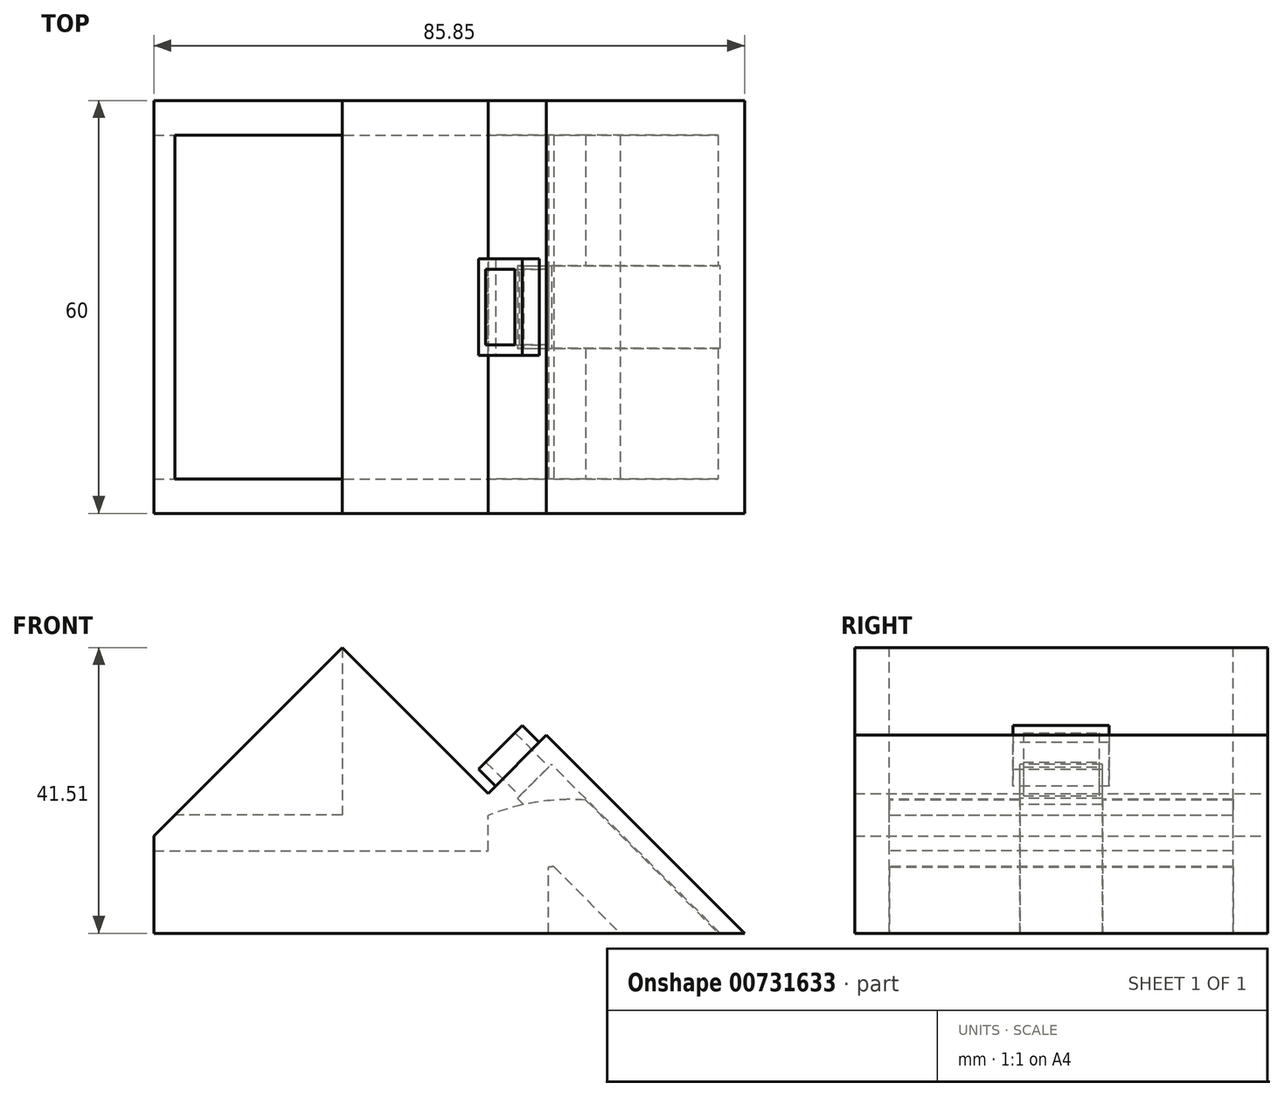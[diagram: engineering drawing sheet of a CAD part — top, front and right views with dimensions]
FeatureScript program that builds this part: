
annotation { "Feature Type Name" : "Feature", "Feature Type Description" : "" }
export const myFeature = defineFeature(function(context is Context, id is Id, definition is map)
    precondition{}
    {
        {
            var Q0;
            Q0=qCreatedBy(makeId("Front.planeOp"),FACE);
            var sketch = newSketch(context, id + "F0", { "sketchPlane" : qUnion([Q0])});
            skLineSegment(sketch, "E0", {"start": v(-35.85, 14.15) * mm, "end": v(-8.49, 41.51) * mm});
            skLineSegment(sketch, "E1", {"start": v(21.21, 28.79) * mm, "end": v(50, 0) * mm});
            skLineSegment(sketch, "E2", {"start": v(50, 0) * mm, "end": v(-35.85, 0) * mm});
            skLineSegment(sketch, "E3", {"start": v(-8.49, 41.51) * mm, "end": v(12.73, 20.3) * mm});
            skLineSegment(sketch, "E4", {"start": v(12.73, 20.3) * mm, "end": v(21.21, 28.79) * mm});
            skLineSegment(sketch, "E5", {"start": v(-35.85, 0) * mm, "end": v(-35.85, 14.15) * mm});
            skSolve(sketch);
        }
        {
            var Q0;
            Q0 = qSketchRegion(id + "F0", true);
            extrude(context, id + "F1", {"entities" : qUnion([Q0]), "endBound" : BoundingType.SYMMETRIC, "depth" : 60 * mm, "offsetDistance" : 25 * mm});
        }
        {
            var Q0;
            Q0=makeQuery(id+"F1.opExtrude","SWEPT_FACE",FACE,{"disambiguationData":[OSD([sQuery(id+"F0.wireOp",EDGE,"E4")])]});
            var sketch = newSketch(context, id + "F2", { "sketchPlane" : qUnion([Q0])});
            skPoint(sketch, "E6.middle.positionSnap0", {"position": v(0, 23.36) * mm});
            skPoint(sketch, "E6.centerSnap0", {"position": v(0, 23.36) * mm});
            skLineSegment(sketch, "E7.bottom", {"start": v(6, 32.86) * mm, "end": v(-6, 32.86) * mm});
            skLineSegment(sketch, "E7.top", {"start": v(6, 25.86) * mm, "end": v(-6, 25.86) * mm});
            skLineSegment(sketch, "E7.left", {"start": v(6, 32.86) * mm, "end": v(6, 25.86) * mm});
            skLineSegment(sketch, "E7.right", {"start": v(-6, 32.86) * mm, "end": v(-6, 25.86) * mm});
            skPoint(sketch, "E7.middle", {"position": v(0, 29.36) * mm});
            skPoint(sketch, "E7.middle.positionSnap0", {"position": v(-30, 29.36) * mm});
            skPoint(sketch, "E7.centerSnap0", {"position": v(-30, 29.36) * mm});
            skSolve(sketch);
        }
        {
            var Q0;
            Q0 = qSketchRegion(id + "F2", true);
            extrude(context, id + "F3", {"entities" : qUnion([Q0]), "operationType" : NewBodyOperationType.REMOVE, "endBound" : BoundingType.UP_TO_NEXT, "oppositeDirection" : true, "depth" : 25 * mm, "offsetDistance" : 25 * mm});
        }
        {
            var Q0;
            Q0=qCreatedBy(makeId("Front.planeOp"),FACE);
            var sketch = newSketch(context, id + "F4", { "sketchPlane" : qUnion([Q0])});
            skLineSegment(sketch, "E8", {"start": v(46.17, 0) * mm, "end": v(26.91, 19.37) * mm});
            skLineSegment(sketch, "E9", {"start": v(22.27, 9.69) * mm, "end": v(31.9, 0) * mm});
            skArc(sketch, "E10", {"start": v(22.27, 9.69) * mm, "mid": v(17.31, 8.57) * mm, "end": v(12.73, 6.4) * mm});
            skPoint(sketch, "E10.startSnap0", {"position": v(36.54, 9.69) * mm});
            skArc(sketch, "E11", {"start": v(26.91, 19.37) * mm, "mid": v(19.7, 19.04) * mm, "end": v(12.75, 17.13) * mm});
            skLineSegment(sketch, "E12", {"start": v(12.73, 6.4) * mm, "end": v(12.75, 17.13) * mm});
            skLineSegment(sketch, "E13", {"start": v(31.9, 0) * mm, "end": v(46.17, 0) * mm});
            skSolve(sketch);
        }
        {
            var Q0;
            Q0 = qSketchRegion(id + "F4", true);
            extrude(context, id + "F5", {"entities" : qUnion([Q0]), "operationType" : NewBodyOperationType.REMOVE, "endBound" : BoundingType.SYMMETRIC, "oppositeDirection" : true, "depth" : 50 * mm, "offsetDistance" : 25 * mm});
        }
        {
            var Q0;
            Q0=qCreatedBy(makeId("Front.planeOp"),FACE);
            var sketch = newSketch(context, id + "F6", { "sketchPlane" : qUnion([Q0])});
            skLineSegment(sketch, "E14.bottom", {"start": v(-39.37, 0) * mm, "end": v(21.51, 0) * mm});
            skLineSegment(sketch, "E14.top", {"start": v(-39.37, 11.95) * mm, "end": v(21.51, 11.95) * mm});
            skLineSegment(sketch, "E14.left", {"start": v(-39.37, 0) * mm, "end": v(-39.37, 11.95) * mm});
            skLineSegment(sketch, "E14.right", {"start": v(21.51, 0) * mm, "end": v(21.51, 11.95) * mm});
            skSolve(sketch);
        }
        {
            var Q0;
            Q0 = qSketchRegion(id + "F6", true);
            extrude(context, id + "F7", {"entities" : qUnion([Q0]), "operationType" : NewBodyOperationType.REMOVE, "endBound" : BoundingType.SYMMETRIC, "oppositeDirection" : true, "depth" : 50 * mm, "offsetDistance" : 25 * mm});
        }
        {
            var Q0;
            Q0=makeQuery(id+"F1.opExtrude","SWEPT_FACE",FACE,{"disambiguationData":[OSD([sQuery(id+"F0.wireOp",EDGE,"E4")])]});
            var sketch = newSketch(context, id + "F8", { "sketchPlane" : qUnion([Q0])});
            skLineSegment(sketch, "E15.bottom", {"start": v(5.5, 32.36) * mm, "end": v(-5.5, 32.36) * mm});
            skLineSegment(sketch, "E15.top", {"start": v(5.5, 26.36) * mm, "end": v(-5.5, 26.36) * mm});
            skLineSegment(sketch, "E15.left", {"start": v(5.5, 32.36) * mm, "end": v(5.5, 26.36) * mm});
            skLineSegment(sketch, "E15.right", {"start": v(-5.5, 32.36) * mm, "end": v(-5.5, 26.36) * mm});
            skPoint(sketch, "E15.middle", {"position": v(0, 29.36) * mm});
            skPoint(sketch, "E15.middle.positionSnap0", {"position": v(-6, 29.36) * mm});
            skPoint(sketch, "E15.middle.positionSnap1", {"position": v(0, 23.36) * mm});
            skPoint(sketch, "E15.centerSnap0", {"position": v(-6, 29.36) * mm});
            skPoint(sketch, "E15.centerSnap1", {"position": v(0, 23.36) * mm});
            skLineSegment(sketch, "E16.0", {"start": v(7, 33.86) * mm, "end": v(-7, 33.86) * mm});
            skLineSegment(sketch, "E16.1", {"start": v(7, 33.86) * mm, "end": v(7, 24.86) * mm});
            skLineSegment(sketch, "E16.2", {"start": v(7, 24.86) * mm, "end": v(-7, 24.86) * mm});
            skLineSegment(sketch, "E16.3", {"start": v(-7, 33.86) * mm, "end": v(-7, 24.86) * mm});
            skSolve(sketch);
        }
        {
            var Q0;
            Q0 = qSketchRegion(id + "F8", true);
            extrude(context, id + "F9", {"entities" : qUnion([Q0]), "operationType" : NewBodyOperationType.ADD, "endBound" : BoundingType.SYMMETRIC, "depth" : 7 * mm, "offsetDistance" : 25 * mm});
        }
        {
            var Q0;
            Q0=qCreatedBy(makeId("Front.planeOp"),FACE);
            var sketch = newSketch(context, id + "F10", { "sketchPlane" : qUnion([Q0])});
            skLineSegment(sketch, "E17.bottom", {"start": v(-8.49, 41.52) * mm, "end": v(-50.03, 41.52) * mm});
            skLineSegment(sketch, "E17.top", {"start": v(-8.49, 17.18) * mm, "end": v(-50.03, 17.18) * mm});
            skLineSegment(sketch, "E17.left", {"start": v(-8.49, 41.52) * mm, "end": v(-8.49, 17.18) * mm});
            skLineSegment(sketch, "E17.right", {"start": v(-50.03, 41.52) * mm, "end": v(-50.03, 17.18) * mm});
            skSolve(sketch);
        }
        {
            var Q0;
            Q0 = qSketchRegion(id + "F10", true);
            extrude(context, id + "F11", {"entities" : qUnion([Q0]), "operationType" : NewBodyOperationType.REMOVE, "endBound" : BoundingType.SYMMETRIC, "oppositeDirection" : true, "depth" : 50 * mm, "offsetDistance" : 25 * mm});
        }
    });
